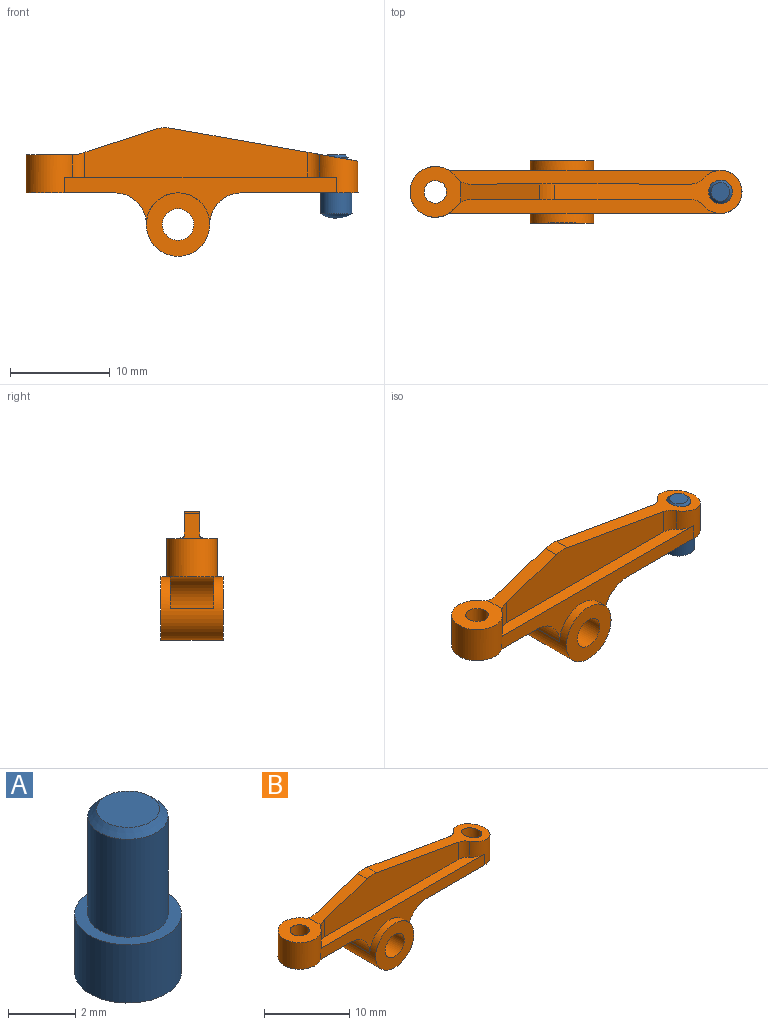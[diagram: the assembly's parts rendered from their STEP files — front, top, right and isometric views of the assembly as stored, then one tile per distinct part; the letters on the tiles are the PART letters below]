
ASSEMBLY  parts=2 mates=1
PART A: 6 faces, bbox 3.2x3.2x6.4 mm
  f0: sphere r=3.17mm, area 8.5mm2, adj f1
  f1: cylinder r=1.59mm len=3.18mm, axis (0,0,-1), area 21.1mm2, adj f0,f2
  f2: plane 3.18x3.18mm, normal (0,0,1), area 3.5mm2, adj f1,f3
  f3: cylinder r=1.19mm len=3.56mm, axis (0,0,-1), area 26.6mm2, adj f2,f5
  f4: plane 1.87x1.87mm, normal (0,0,1), area 2.8mm2, adj f5
  f5: cone r=1.19mm half-angle=45deg, axis (0,0,-1), area 2.4mm2, adj f3,f4
PART B: 26 faces, bbox 33.4x6.3x13 mm
  f0: plane 11.68x4.32mm, normal (0,0,-1), area 44mm2, adj f3,f11,f13,f14,f20
  f1: plane 8.89x5.08mm, normal (0,0,-1), area 34.2mm2, adj f2,f11,f13,f15,f21
  f2: cylinder r=2.54mm len=5.08mm, axis (0,0,-1), area 45.7mm2, adj f1,f9,f10,f11,f12,f13,f22,f23
  f3: cylinder r=2.16mm len=4.32mm, axis (0,0,-1), area 30.6mm2, adj f0,f8,f10,f11,f12,f13,f24,f25
  f4: plane 22.3x4.96mm, normal (0,1,0), area 84.1mm2, adj f6,f7,f8,f12,f22,f25
  f5: plane 22.3x4.96mm, normal (0,-1,0), area 84.1mm2, adj f6,f7,f8,f10,f23,f24
  f6: plane 7.91x2.58mm, normal (-0.31,0,0.95), area 13.2mm2, adj f4,f5,f7,f9,f22,f23
  f7: cylinder r=3.17mm len=1.58mm, axis (0,-1,0), area 2.4mm2, adj f4,f5,f6,f8
  f8: plane 18.85x4.41mm, normal (0.17,0,0.98), area 33.7mm2, adj f3,f4,f5,f7,f20,f24,f25
  f9: plane 5.08x5.08mm, normal (0,0,1), area 16.5mm2, adj f2,f6,f21,f22,f23
  f10: plane 27.24x1.37mm, normal (0,0,1), area 34.2mm2, adj f2,f3,f5,f11,f23,f24
  f11: plane 27.24x4.75mm, normal (0,-1,0), area 51.5mm2, adj f0,f1,f2,f3,f10,f14,f15,f16
  f12: plane 27.24x1.37mm, normal (0,0,1), area 34.2mm2, adj f2,f3,f4,f13,f22,f25
  f13: plane 27.24x4.75mm, normal (0,1,0), area 51.5mm2, adj f0,f1,f2,f3,f12,f14,f15,f16
  f14: cylinder r=3.17mm len=4.32mm, axis (0,1,0), area 21.5mm2, adj f0,f11,f13,f16
  f15: cylinder r=3.17mm len=4.32mm, axis (0,1,0), area 21.5mm2, adj f1,f11,f13,f16
  f16: cylinder r=3.17mm len=6.35mm, axis (0,1,0), area 81.1mm2, adj f11,f13,f14,f15,f17,f18
  f17: plane 6.35x6.35mm, normal (0,1,0), area 23.8mm2, adj f16,f19
  f18: plane 6.35x6.35mm, normal (0,-1,0), area 23.8mm2, adj f16,f19
  f19: cylinder r=1.59mm len=6.22mm, axis (0,-1,0), area 62.1mm2, adj f17,f18
  f20: cylinder r=1.19mm len=3.77mm, axis (0,0,-1), area 26.6mm2, adj f0,f8
  f21: cylinder r=1.13mm len=3.81mm, axis (0,0,-1), area 27.1mm2, adj f1,f9
  f22: cylinder r=1.59mm len=2.51mm, axis (0,0,-1), area 3.5mm2, adj f2,f4,f6,f9,f12
  f23: cylinder r=1.59mm len=2.51mm, axis (0,0,-1), area 3.5mm2, adj f2,f5,f6,f9,f10
  f24: cylinder r=1.59mm len=2.49mm, axis (0,0,-1), area 3.3mm2, adj f3,f5,f8,f10
  f25: cylinder r=1.59mm len=2.49mm, axis (0,0,-1), area 3.3mm2, adj f3,f4,f8,f12
PLACE A t=(15.88,0,3.18)mm
PLACE B t=(0,0,3.18)mm fixed
MATE fastened A.f1 <-> B.f20  axis (0,0,1) through (15.88,0,3.18)mm
